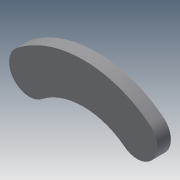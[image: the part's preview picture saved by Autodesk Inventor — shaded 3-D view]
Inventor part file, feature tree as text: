
AUTODESK INVENTOR PART (.ipt)
format: ipt  version: 2013 (Build 170138000, 138)  size: 98,816 bytes
history: native  units: mm
features: extrude x2, sketch x2
ambient origin geometry x8: Origin, YZ Plane, XZ Plane, XY Plane, X Axis, Y Axis, Z Axis, Center Point
bodies: Solid1 (feature_tree)
feature tree (4):
  extrude  "Extrusion1"  Depth=6.0mm
  extrude  "Extrusion2"  Depth=3.0mm
  sketch  "Sketch1"  dims[d13=16.0mm d14=6.0mm]
  sketch  "Sketch2"  dims[d16=6.0mm d17=3.0mm d18=3.0mm d19=2.0mm d20=0.0mm d21=0.1mm d22=0.1mm d23=2.0mm d24=0.0mm]
